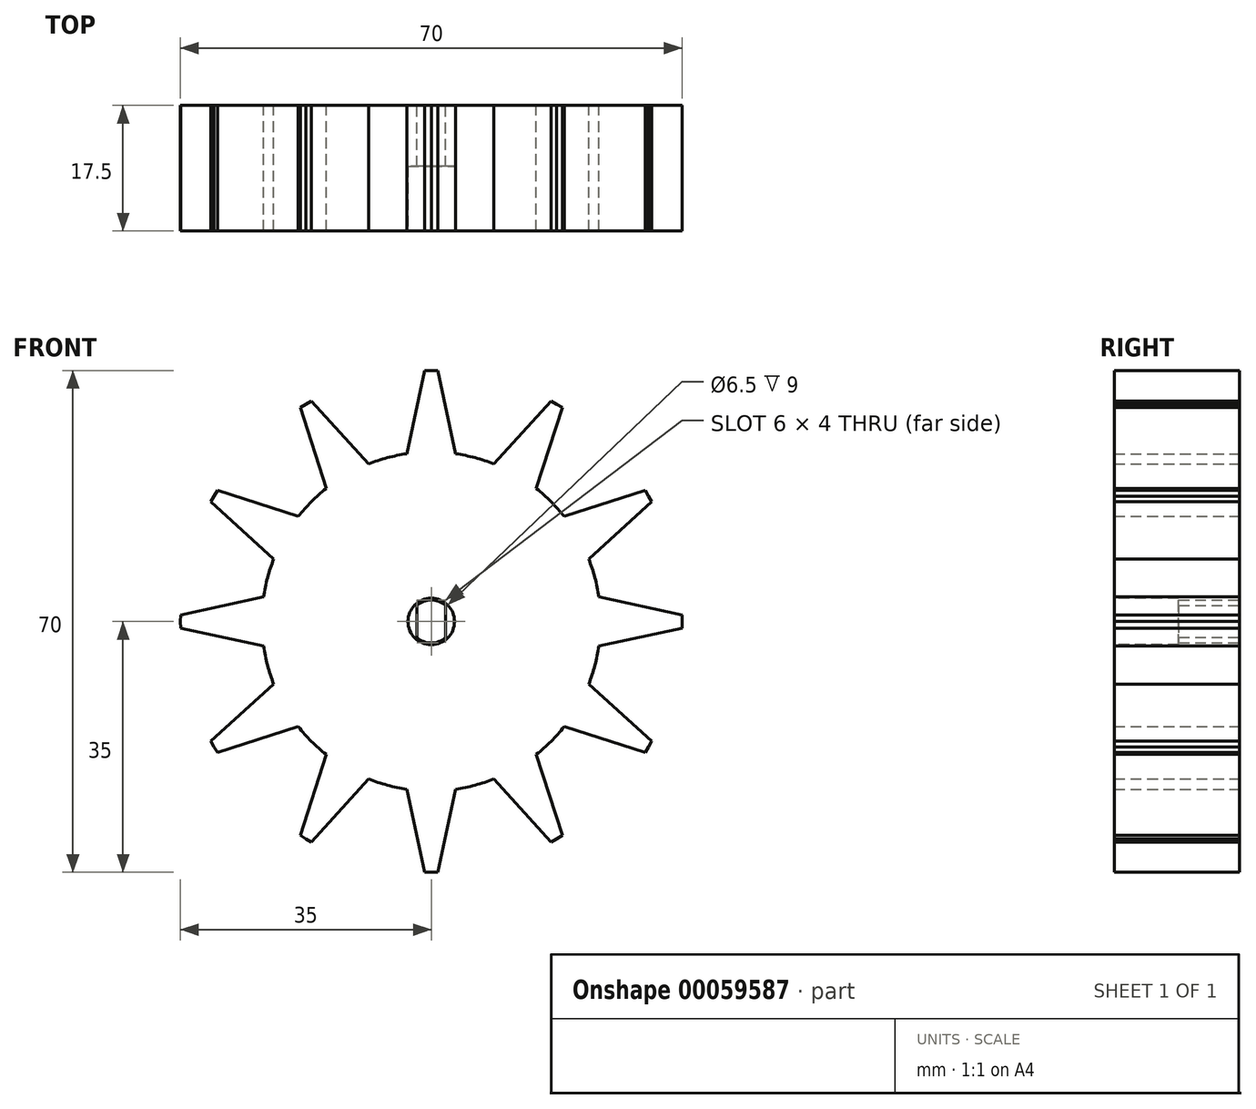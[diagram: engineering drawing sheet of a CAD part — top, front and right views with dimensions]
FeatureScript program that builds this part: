
annotation { "Feature Type Name" : "Feature", "Feature Type Description" : "" }
export const myFeature = defineFeature(function(context is Context, id is Id, definition is map)
    precondition{}
    {
        {
            var Q0;
            Q0=qCreatedBy(makeId("Front.planeOp"),FACE);
            var sketch = newSketch(context, id + "F0", { "sketchPlane" : qUnion([Q0])});
            skLineSegment(sketch, "E0", {"start": v(0, 0) * mm, "end": v(0, 35) * mm, "construction": true});
            skPoint(sketch, "E1.MirrorP", {"position": v(0, 35) * mm});
            skCircle(sketch, "E2", {"center": v(0, 0) * mm, "radius": 23.65 * mm});
            skCircle(sketch, "E3", {"center": v(0, 0) * mm, "radius": 35 * mm, "construction": true});
            skCircle(sketch, "E4", {"center": v(0, 0) * mm, "radius": 30 * mm, "construction": true});
            skLineSegment(sketch, "E5", {"start": v(0, 35) * mm, "end": v(0.91, 34.99) * mm});
            skLineSegment(sketch, "E6", {"start": v(0.91, 34.99) * mm, "end": v(3.42, 23.4) * mm});
            skLineSegment(sketch, "E7.MirrorCS", {"start": v(0, 35) * mm, "end": v(-0.91, 34.99) * mm});
            skLineSegment(sketch, "E8.MirrorCS", {"start": v(-0.91, 34.99) * mm, "end": v(-3.42, 23.4) * mm});
            skPoint(sketch, "E9.1.0", {"position": v(-17.5, 30.31) * mm});
            skLineSegment(sketch, "E9.1.1", {"start": v(-17.5, 30.31) * mm, "end": v(-16.7, 30.76) * mm});
            skLineSegment(sketch, "E9.1.2", {"start": v(-17.5, 30.31) * mm, "end": v(-18.29, 29.84) * mm});
            skLineSegment(sketch, "E9.1.3", {"start": v(-16.7, 30.76) * mm, "end": v(-8.74, 21.98) * mm});
            skLineSegment(sketch, "E9.1.4", {"start": v(-18.29, 29.84) * mm, "end": v(-14.66, 18.56) * mm});
            skPoint(sketch, "E9.2.0", {"position": v(-30.31, 17.5) * mm});
            skLineSegment(sketch, "E9.2.1", {"start": v(-30.31, 17.5) * mm, "end": v(-29.84, 18.29) * mm});
            skLineSegment(sketch, "E9.2.2", {"start": v(-30.31, 17.5) * mm, "end": v(-30.76, 16.7) * mm});
            skLineSegment(sketch, "E9.2.3", {"start": v(-29.84, 18.29) * mm, "end": v(-18.56, 14.66) * mm});
            skLineSegment(sketch, "E9.2.4", {"start": v(-30.76, 16.7) * mm, "end": v(-21.98, 8.74) * mm});
            skPoint(sketch, "E9.3.0", {"position": v(-35, 0) * mm});
            skLineSegment(sketch, "E9.3.1", {"start": v(-35, 0) * mm, "end": v(-34.99, 0.91) * mm});
            skLineSegment(sketch, "E9.3.2", {"start": v(-35, 0) * mm, "end": v(-34.99, -0.91) * mm});
            skLineSegment(sketch, "E9.3.3", {"start": v(-34.99, 0.91) * mm, "end": v(-23.4, 3.42) * mm});
            skLineSegment(sketch, "E9.3.4", {"start": v(-34.99, -0.91) * mm, "end": v(-23.4, -3.42) * mm});
            skPoint(sketch, "E9.4.0", {"position": v(-30.31, -17.5) * mm});
            skLineSegment(sketch, "E9.4.1", {"start": v(-30.31, -17.5) * mm, "end": v(-30.76, -16.7) * mm});
            skLineSegment(sketch, "E9.4.2", {"start": v(-30.31, -17.5) * mm, "end": v(-29.84, -18.29) * mm});
            skLineSegment(sketch, "E9.4.3", {"start": v(-30.76, -16.7) * mm, "end": v(-21.98, -8.74) * mm});
            skLineSegment(sketch, "E9.4.4", {"start": v(-29.84, -18.29) * mm, "end": v(-18.56, -14.66) * mm});
            skPoint(sketch, "E9.5.0", {"position": v(-17.5, -30.31) * mm});
            skLineSegment(sketch, "E9.5.1", {"start": v(-17.5, -30.31) * mm, "end": v(-18.29, -29.84) * mm});
            skLineSegment(sketch, "E9.5.2", {"start": v(-17.5, -30.31) * mm, "end": v(-16.7, -30.76) * mm});
            skLineSegment(sketch, "E9.5.3", {"start": v(-18.29, -29.84) * mm, "end": v(-14.66, -18.56) * mm});
            skLineSegment(sketch, "E9.5.4", {"start": v(-16.7, -30.76) * mm, "end": v(-8.74, -21.98) * mm});
            skPoint(sketch, "E9.6.0", {"position": v(0, -35) * mm});
            skLineSegment(sketch, "E9.6.1", {"start": v(0, -35) * mm, "end": v(-0.91, -34.99) * mm});
            skLineSegment(sketch, "E9.6.2", {"start": v(0, -35) * mm, "end": v(0.91, -34.99) * mm});
            skLineSegment(sketch, "E9.6.3", {"start": v(-0.91, -34.99) * mm, "end": v(-3.42, -23.4) * mm});
            skLineSegment(sketch, "E9.6.4", {"start": v(0.91, -34.99) * mm, "end": v(3.42, -23.4) * mm});
            skPoint(sketch, "E9.7.0", {"position": v(17.5, -30.31) * mm});
            skLineSegment(sketch, "E9.7.1", {"start": v(17.5, -30.31) * mm, "end": v(16.7, -30.76) * mm});
            skLineSegment(sketch, "E9.7.2", {"start": v(17.5, -30.31) * mm, "end": v(18.29, -29.84) * mm});
            skLineSegment(sketch, "E9.7.3", {"start": v(16.7, -30.76) * mm, "end": v(8.74, -21.98) * mm});
            skLineSegment(sketch, "E9.7.4", {"start": v(18.29, -29.84) * mm, "end": v(14.66, -18.56) * mm});
            skPoint(sketch, "E9.8.0", {"position": v(30.31, -17.5) * mm});
            skLineSegment(sketch, "E9.8.1", {"start": v(30.31, -17.5) * mm, "end": v(29.84, -18.29) * mm});
            skLineSegment(sketch, "E9.8.2", {"start": v(30.31, -17.5) * mm, "end": v(30.76, -16.7) * mm});
            skLineSegment(sketch, "E9.8.3", {"start": v(29.84, -18.29) * mm, "end": v(18.56, -14.66) * mm});
            skLineSegment(sketch, "E9.8.4", {"start": v(30.76, -16.7) * mm, "end": v(21.98, -8.74) * mm});
            skPoint(sketch, "E9.9.0", {"position": v(35, 0) * mm});
            skLineSegment(sketch, "E9.9.1", {"start": v(35, 0) * mm, "end": v(34.99, -0.91) * mm});
            skLineSegment(sketch, "E9.9.2", {"start": v(35, 0) * mm, "end": v(34.99, 0.91) * mm});
            skLineSegment(sketch, "E9.9.3", {"start": v(34.99, -0.91) * mm, "end": v(23.4, -3.42) * mm});
            skLineSegment(sketch, "E9.9.4", {"start": v(34.99, 0.91) * mm, "end": v(23.4, 3.42) * mm});
            skPoint(sketch, "E9.10.0", {"position": v(30.31, 17.5) * mm});
            skLineSegment(sketch, "E9.10.1", {"start": v(30.31, 17.5) * mm, "end": v(30.76, 16.7) * mm});
            skLineSegment(sketch, "E9.10.2", {"start": v(30.31, 17.5) * mm, "end": v(29.84, 18.29) * mm});
            skLineSegment(sketch, "E9.10.3", {"start": v(30.76, 16.7) * mm, "end": v(21.98, 8.74) * mm});
            skLineSegment(sketch, "E9.10.4", {"start": v(29.84, 18.29) * mm, "end": v(18.56, 14.66) * mm});
            skPoint(sketch, "E9.11.0", {"position": v(17.5, 30.31) * mm});
            skLineSegment(sketch, "E9.11.1", {"start": v(17.5, 30.31) * mm, "end": v(18.29, 29.84) * mm});
            skLineSegment(sketch, "E9.11.2", {"start": v(17.5, 30.31) * mm, "end": v(16.7, 30.76) * mm});
            skLineSegment(sketch, "E9.11.3", {"start": v(18.29, 29.84) * mm, "end": v(14.66, 18.56) * mm});
            skLineSegment(sketch, "E9.11.4", {"start": v(16.7, 30.76) * mm, "end": v(8.74, 21.98) * mm});
            skSolve(sketch);
        }
        {
            var Q0;
            Q0=qSketchRegion(id+"F0",true);
            extrude(context, id + "F1", {"entities" : qUnion([Q0]), "depth" : 17.5 * mm});
        }
        {
            var Q0;
            Q0=makeQuery(id+"F1.opExtrude","CAP_FACE",FACE,{"disambiguationData":[OSD([sQuery(id+"F0.wireOp",EDGE,"ocoJJeUB-d1Um-W4kJ-qDCv-TqZqPxDJkEKx"),sQuery(id+"F0.wireOp",EDGE,"b6f91543-6248-4149-b9b5-be24c7ea4c220.MirrorCS"),sQuery(id+"F0.wireOp",EDGE,"E2"),sQuery(id+"F0.wireOp",EDGE,"JOJCOvuX-G6uY-4Be6-6DYf-OOnBLEOs56iL"),sQuery(id+"F0.wireOp",EDGE,"41t5yxBz-pZFD-voqE-dTbU-a2C4DeACViRG"),sQuery(id+"F0.wireOp",EDGE,"168a9aca-b7f7-43cf-8ef5-aee35012c7f2.1.1"),sQuery(id+"F0.wireOp",EDGE,"168a9aca-b7f7-43cf-8ef5-aee35012c7f2.1.3"),sQuery(id+"F0.wireOp",EDGE,"168a9aca-b7f7-43cf-8ef5-aee35012c7f2.1.7"),sQuery(id+"F0.wireOp",EDGE,"168a9aca-b7f7-43cf-8ef5-aee35012c7f2.1.8"),sQuery(id+"F0.wireOp",EDGE,"168a9aca-b7f7-43cf-8ef5-aee35012c7f2.2.1"),sQuery(id+"F0.wireOp",EDGE,"168a9aca-b7f7-43cf-8ef5-aee35012c7f2.2.3"),sQuery(id+"F0.wireOp",EDGE,"168a9aca-b7f7-43cf-8ef5-aee35012c7f2.2.7"),sQuery(id+"F0.wireOp",EDGE,"168a9aca-b7f7-43cf-8ef5-aee35012c7f2.2.8"),sQuery(id+"F0.wireOp",EDGE,"168a9aca-b7f7-43cf-8ef5-aee35012c7f2.3.1"),sQuery(id+"F0.wireOp",EDGE,"168a9aca-b7f7-43cf-8ef5-aee35012c7f2.3.3"),sQuery(id+"F0.wireOp",EDGE,"168a9aca-b7f7-43cf-8ef5-aee35012c7f2.3.7"),sQuery(id+"F0.wireOp",EDGE,"168a9aca-b7f7-43cf-8ef5-aee35012c7f2.3.8"),sQuery(id+"F0.wireOp",EDGE,"168a9aca-b7f7-43cf-8ef5-aee35012c7f2.4.1"),sQuery(id+"F0.wireOp",EDGE,"168a9aca-b7f7-43cf-8ef5-aee35012c7f2.4.3"),sQuery(id+"F0.wireOp",EDGE,"168a9aca-b7f7-43cf-8ef5-aee35012c7f2.4.7"),sQuery(id+"F0.wireOp",EDGE,"168a9aca-b7f7-43cf-8ef5-aee35012c7f2.4.8"),sQuery(id+"F0.wireOp",EDGE,"168a9aca-b7f7-43cf-8ef5-aee35012c7f2.5.1"),sQuery(id+"F0.wireOp",EDGE,"168a9aca-b7f7-43cf-8ef5-aee35012c7f2.5.3"),sQuery(id+"F0.wireOp",EDGE,"168a9aca-b7f7-43cf-8ef5-aee35012c7f2.5.7"),sQuery(id+"F0.wireOp",EDGE,"168a9aca-b7f7-43cf-8ef5-aee35012c7f2.5.8"),sQuery(id+"F0.wireOp",EDGE,"168a9aca-b7f7-43cf-8ef5-aee35012c7f2.6.1"),sQuery(id+"F0.wireOp",EDGE,"168a9aca-b7f7-43cf-8ef5-aee35012c7f2.6.3"),sQuery(id+"F0.wireOp",EDGE,"168a9aca-b7f7-43cf-8ef5-aee35012c7f2.6.7"),sQuery(id+"F0.wireOp",EDGE,"168a9aca-b7f7-43cf-8ef5-aee35012c7f2.6.8"),sQuery(id+"F0.wireOp",EDGE,"168a9aca-b7f7-43cf-8ef5-aee35012c7f2.7.1"),sQuery(id+"F0.wireOp",EDGE,"168a9aca-b7f7-43cf-8ef5-aee35012c7f2.7.3"),sQuery(id+"F0.wireOp",EDGE,"168a9aca-b7f7-43cf-8ef5-aee35012c7f2.7.7"),sQuery(id+"F0.wireOp",EDGE,"168a9aca-b7f7-43cf-8ef5-aee35012c7f2.7.8"),sQuery(id+"F0.wireOp",EDGE,"168a9aca-b7f7-43cf-8ef5-aee35012c7f2.8.1"),sQuery(id+"F0.wireOp",EDGE,"168a9aca-b7f7-43cf-8ef5-aee35012c7f2.8.3"),sQuery(id+"F0.wireOp",EDGE,"168a9aca-b7f7-43cf-8ef5-aee35012c7f2.8.7"),sQuery(id+"F0.wireOp",EDGE,"168a9aca-b7f7-43cf-8ef5-aee35012c7f2.8.8"),sQuery(id+"F0.wireOp",EDGE,"168a9aca-b7f7-43cf-8ef5-aee35012c7f2.9.1"),sQuery(id+"F0.wireOp",EDGE,"168a9aca-b7f7-43cf-8ef5-aee35012c7f2.9.3"),sQuery(id+"F0.wireOp",EDGE,"168a9aca-b7f7-43cf-8ef5-aee35012c7f2.9.7"),sQuery(id+"F0.wireOp",EDGE,"168a9aca-b7f7-43cf-8ef5-aee35012c7f2.9.8"),sQuery(id+"F0.wireOp",EDGE,"168a9aca-b7f7-43cf-8ef5-aee35012c7f2.10.1"),sQuery(id+"F0.wireOp",EDGE,"168a9aca-b7f7-43cf-8ef5-aee35012c7f2.10.3"),sQuery(id+"F0.wireOp",EDGE,"168a9aca-b7f7-43cf-8ef5-aee35012c7f2.10.7"),sQuery(id+"F0.wireOp",EDGE,"168a9aca-b7f7-43cf-8ef5-aee35012c7f2.10.8"),sQuery(id+"F0.wireOp",EDGE,"168a9aca-b7f7-43cf-8ef5-aee35012c7f2.11.1"),sQuery(id+"F0.wireOp",EDGE,"168a9aca-b7f7-43cf-8ef5-aee35012c7f2.11.3"),sQuery(id+"F0.wireOp",EDGE,"168a9aca-b7f7-43cf-8ef5-aee35012c7f2.11.7"),sQuery(id+"F0.wireOp",EDGE,"168a9aca-b7f7-43cf-8ef5-aee35012c7f2.11.8")])],"isStart":true});
            var sketch = newSketch(context, id + "F2", { "sketchPlane" : qUnion([Q0])});
            skArc(sketch, "E10", {"start": v(2, 2.24) * mm, "mid": v(0, 3) * mm, "end": v(-2, 2.24) * mm});
            skLineSegment(sketch, "E11.left", {"start": v(-2, 2.24) * mm, "end": v(-2, -2.24) * mm});
            skLineSegment(sketch, "E11.right", {"start": v(2, 2.24) * mm, "end": v(2, -2.24) * mm});
            skArc(sketch, "E12.trimOffspring", {"start": v(-2, -2.24) * mm, "mid": v(0, -3) * mm, "end": v(2, -2.24) * mm});
            skSolve(sketch);
        }
        {
            var Q0;
            Q0=qSketchRegion(id+"F2",true);
            extrude(context, id + "F3", {"entities" : qUnion([Q0]), "operationType" : NewBodyOperationType.REMOVE, "oppositeDirection" : true, "depth" : 9 * mm});
        }
        {
            var Q0;
            Q0=makeQuery(id+"F1.opExtrude","CAP_FACE",FACE,{"disambiguationData":[OSD([sQuery(id+"F0.wireOp",EDGE,"ocoJJeUB-d1Um-W4kJ-qDCv-TqZqPxDJkEKx"),sQuery(id+"F0.wireOp",EDGE,"b6f91543-6248-4149-b9b5-be24c7ea4c220.MirrorCS"),sQuery(id+"F0.wireOp",EDGE,"E2"),sQuery(id+"F0.wireOp",EDGE,"JOJCOvuX-G6uY-4Be6-6DYf-OOnBLEOs56iL"),sQuery(id+"F0.wireOp",EDGE,"41t5yxBz-pZFD-voqE-dTbU-a2C4DeACViRG"),sQuery(id+"F0.wireOp",EDGE,"168a9aca-b7f7-43cf-8ef5-aee35012c7f2.1.1"),sQuery(id+"F0.wireOp",EDGE,"168a9aca-b7f7-43cf-8ef5-aee35012c7f2.1.3"),sQuery(id+"F0.wireOp",EDGE,"168a9aca-b7f7-43cf-8ef5-aee35012c7f2.1.7"),sQuery(id+"F0.wireOp",EDGE,"168a9aca-b7f7-43cf-8ef5-aee35012c7f2.1.8"),sQuery(id+"F0.wireOp",EDGE,"168a9aca-b7f7-43cf-8ef5-aee35012c7f2.2.1"),sQuery(id+"F0.wireOp",EDGE,"168a9aca-b7f7-43cf-8ef5-aee35012c7f2.2.3"),sQuery(id+"F0.wireOp",EDGE,"168a9aca-b7f7-43cf-8ef5-aee35012c7f2.2.7"),sQuery(id+"F0.wireOp",EDGE,"168a9aca-b7f7-43cf-8ef5-aee35012c7f2.2.8"),sQuery(id+"F0.wireOp",EDGE,"168a9aca-b7f7-43cf-8ef5-aee35012c7f2.3.1"),sQuery(id+"F0.wireOp",EDGE,"168a9aca-b7f7-43cf-8ef5-aee35012c7f2.3.3"),sQuery(id+"F0.wireOp",EDGE,"168a9aca-b7f7-43cf-8ef5-aee35012c7f2.3.7"),sQuery(id+"F0.wireOp",EDGE,"168a9aca-b7f7-43cf-8ef5-aee35012c7f2.3.8"),sQuery(id+"F0.wireOp",EDGE,"168a9aca-b7f7-43cf-8ef5-aee35012c7f2.4.1"),sQuery(id+"F0.wireOp",EDGE,"168a9aca-b7f7-43cf-8ef5-aee35012c7f2.4.3"),sQuery(id+"F0.wireOp",EDGE,"168a9aca-b7f7-43cf-8ef5-aee35012c7f2.4.7"),sQuery(id+"F0.wireOp",EDGE,"168a9aca-b7f7-43cf-8ef5-aee35012c7f2.4.8"),sQuery(id+"F0.wireOp",EDGE,"168a9aca-b7f7-43cf-8ef5-aee35012c7f2.5.1"),sQuery(id+"F0.wireOp",EDGE,"168a9aca-b7f7-43cf-8ef5-aee35012c7f2.5.3"),sQuery(id+"F0.wireOp",EDGE,"168a9aca-b7f7-43cf-8ef5-aee35012c7f2.5.7"),sQuery(id+"F0.wireOp",EDGE,"168a9aca-b7f7-43cf-8ef5-aee35012c7f2.5.8"),sQuery(id+"F0.wireOp",EDGE,"168a9aca-b7f7-43cf-8ef5-aee35012c7f2.6.1"),sQuery(id+"F0.wireOp",EDGE,"168a9aca-b7f7-43cf-8ef5-aee35012c7f2.6.3"),sQuery(id+"F0.wireOp",EDGE,"168a9aca-b7f7-43cf-8ef5-aee35012c7f2.6.7"),sQuery(id+"F0.wireOp",EDGE,"168a9aca-b7f7-43cf-8ef5-aee35012c7f2.6.8"),sQuery(id+"F0.wireOp",EDGE,"168a9aca-b7f7-43cf-8ef5-aee35012c7f2.7.1"),sQuery(id+"F0.wireOp",EDGE,"168a9aca-b7f7-43cf-8ef5-aee35012c7f2.7.3"),sQuery(id+"F0.wireOp",EDGE,"168a9aca-b7f7-43cf-8ef5-aee35012c7f2.7.7"),sQuery(id+"F0.wireOp",EDGE,"168a9aca-b7f7-43cf-8ef5-aee35012c7f2.7.8"),sQuery(id+"F0.wireOp",EDGE,"168a9aca-b7f7-43cf-8ef5-aee35012c7f2.8.1"),sQuery(id+"F0.wireOp",EDGE,"168a9aca-b7f7-43cf-8ef5-aee35012c7f2.8.3"),sQuery(id+"F0.wireOp",EDGE,"168a9aca-b7f7-43cf-8ef5-aee35012c7f2.8.7"),sQuery(id+"F0.wireOp",EDGE,"168a9aca-b7f7-43cf-8ef5-aee35012c7f2.8.8"),sQuery(id+"F0.wireOp",EDGE,"168a9aca-b7f7-43cf-8ef5-aee35012c7f2.9.1"),sQuery(id+"F0.wireOp",EDGE,"168a9aca-b7f7-43cf-8ef5-aee35012c7f2.9.3"),sQuery(id+"F0.wireOp",EDGE,"168a9aca-b7f7-43cf-8ef5-aee35012c7f2.9.7"),sQuery(id+"F0.wireOp",EDGE,"168a9aca-b7f7-43cf-8ef5-aee35012c7f2.9.8"),sQuery(id+"F0.wireOp",EDGE,"168a9aca-b7f7-43cf-8ef5-aee35012c7f2.10.1"),sQuery(id+"F0.wireOp",EDGE,"168a9aca-b7f7-43cf-8ef5-aee35012c7f2.10.3"),sQuery(id+"F0.wireOp",EDGE,"168a9aca-b7f7-43cf-8ef5-aee35012c7f2.10.7"),sQuery(id+"F0.wireOp",EDGE,"168a9aca-b7f7-43cf-8ef5-aee35012c7f2.10.8"),sQuery(id+"F0.wireOp",EDGE,"168a9aca-b7f7-43cf-8ef5-aee35012c7f2.11.1"),sQuery(id+"F0.wireOp",EDGE,"168a9aca-b7f7-43cf-8ef5-aee35012c7f2.11.3"),sQuery(id+"F0.wireOp",EDGE,"168a9aca-b7f7-43cf-8ef5-aee35012c7f2.11.7"),sQuery(id+"F0.wireOp",EDGE,"168a9aca-b7f7-43cf-8ef5-aee35012c7f2.11.8")])],"isStart":false});
            var sketch = newSketch(context, id + "F4", { "sketchPlane" : qUnion([Q0])});
            skCircle(sketch, "E13", {"center": v(0, 0) * mm, "radius": 3.25 * mm});
            skSolve(sketch);
        }
        {
            var Q0;
            Q0=qSketchRegion(id+"F4",true);
            extrude(context, id + "F5", {"entities" : qUnion([Q0]), "operationType" : NewBodyOperationType.REMOVE, "oppositeDirection" : true, "depth" : 9 * mm});
        }
    });
